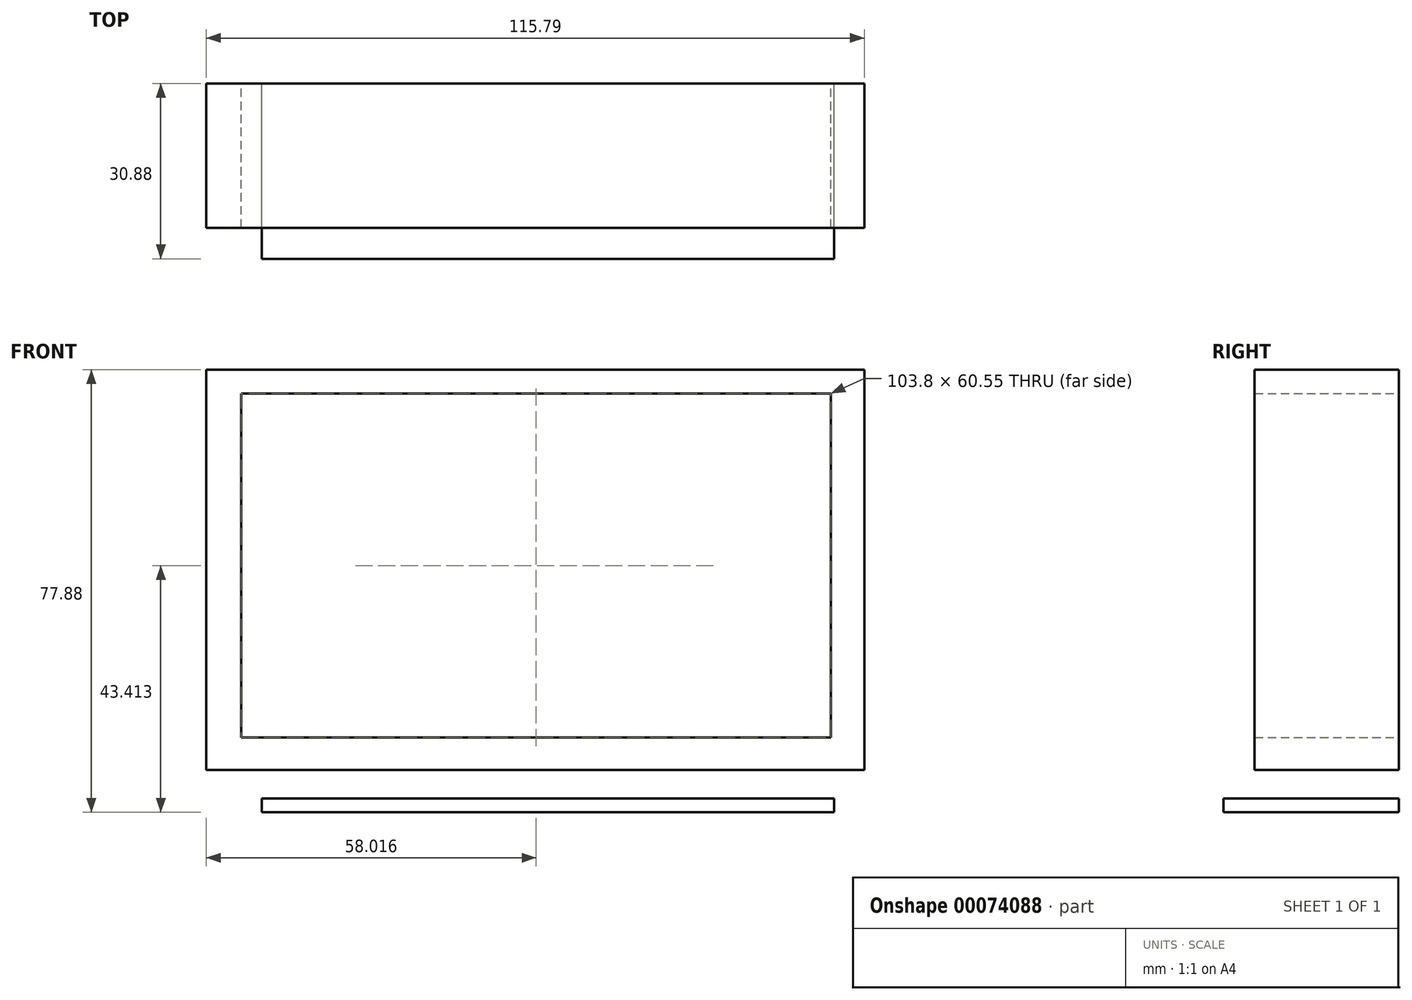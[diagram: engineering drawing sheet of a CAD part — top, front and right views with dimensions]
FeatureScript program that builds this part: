
annotation { "Feature Type Name" : "Feature", "Feature Type Description" : "" }
export const myFeature = defineFeature(function(context is Context, id is Id, definition is map)
    precondition{}
    {
        {
            var Q0;
            Q0=qCreatedBy(makeId("Front.planeOp"),FACE);
            var sketch = newSketch(context, id + "F0", { "sketchPlane" : qUnion([Q0])});
            skLineSegment(sketch, "E0.bottom", {"start": v(-58.2, 41.3) * mm, "end": v(57.59, 41.3) * mm});
            skLineSegment(sketch, "E0.top", {"start": v(-58.2, -29.1) * mm, "end": v(57.59, -29.1) * mm});
            skLineSegment(sketch, "E0.left", {"start": v(-58.2, 41.3) * mm, "end": v(-58.2, -29.1) * mm});
            skLineSegment(sketch, "E0.right", {"start": v(57.59, 41.3) * mm, "end": v(57.59, -29.1) * mm});
            skLineSegment(sketch, "E1.bottom", {"start": v(-26.69, -29.1) * mm, "end": v(30.17, -29.1) * mm});
            skLineSegment(sketch, "E1.top", {"start": v(-26.69, -34.27) * mm, "end": v(30.17, -34.27) * mm});
            skLineSegment(sketch, "E1.left", {"start": v(-26.69, -29.1) * mm, "end": v(-26.69, -34.27) * mm});
            skLineSegment(sketch, "E1.right", {"start": v(30.17, -29.1) * mm, "end": v(30.17, -34.27) * mm});
            skLineSegment(sketch, "E2", {"start": v(-26.69, -34.27) * mm, "end": v(-48.93, -34.27) * mm});
            skLineSegment(sketch, "E3", {"start": v(-48.93, -34.27) * mm, "end": v(30.17, -34.27) * mm});
            skLineSegment(sketch, "E4", {"start": v(30.17, -34.27) * mm, "end": v(50.46, -34.27) * mm});
            skLineSegment(sketch, "E5.bottom", {"start": v(-52.08, 37.12) * mm, "end": v(51.71, 37.12) * mm});
            skLineSegment(sketch, "E5.top", {"start": v(-52.08, -23.43) * mm, "end": v(51.71, -23.43) * mm});
            skLineSegment(sketch, "E5.left", {"start": v(-52.08, 37.12) * mm, "end": v(-52.08, -23.43) * mm});
            skLineSegment(sketch, "E5.right", {"start": v(51.71, 37.12) * mm, "end": v(51.71, -23.43) * mm});
            skSolve(sketch);
        }
        {
            var Q0;
            Q0=makeQuery(id+"F0.imprint","IMPRINT",FACE,{"disambiguationData":[TD([[makeQuery(id+"F0.imprint","IMPRINT",EDGE,{"derivedFrom":sQuery(id+"F0.wireOp",EDGE,"E1.bottom")}),-1.0]])]});
            var Q1;
            Q1=makeQuery(id+"F0.imprint","IMPRINT",FACE,{"disambiguationData":[TD([[makeQuery(id+"F0.imprint","IMPRINT",EDGE,{"derivedFrom":sQuery(id+"F0.wireOp",EDGE,"E0.bottom")}),-1.0]])]});
            extrude(context, id + "F1", {"entities" : qUnion([Q0, Q1]), "depth" : 25.4 * mm});
        }
        {
            var Q0;
            Q0=qCreatedBy(makeId("Front.planeOp"),FACE);
            var sketch = newSketch(context, id + "F2", { "sketchPlane" : qUnion([Q0])});
            skLineSegment(sketch, "E6.bottom", {"start": v(-48.44, -34.14) * mm, "end": v(52.24, -34.14) * mm});
            skLineSegment(sketch, "E6.top", {"start": v(-48.44, -36.57) * mm, "end": v(52.24, -36.57) * mm});
            skLineSegment(sketch, "E6.left", {"start": v(-48.44, -34.14) * mm, "end": v(-48.44, -36.57) * mm});
            skLineSegment(sketch, "E6.right", {"start": v(52.24, -34.14) * mm, "end": v(52.24, -36.57) * mm});
            skSolve(sketch);
        }
        {
            var Q0;
            Q0=makeQuery(id+"F2.imprint","IMPRINT",FACE,{"disambiguationData":[TD([[makeQuery(id+"F2.imprint","IMPRINT",EDGE,{"derivedFrom":sQuery(id+"F2.wireOp",EDGE,"E6.bottom")}),-1.0]])]});
            extrude(context, id + "F3", {"entities" : qUnion([Q0]), "operationType" : NewBodyOperationType.ADD, "depth" : 30.88 * mm});
        }
    });
